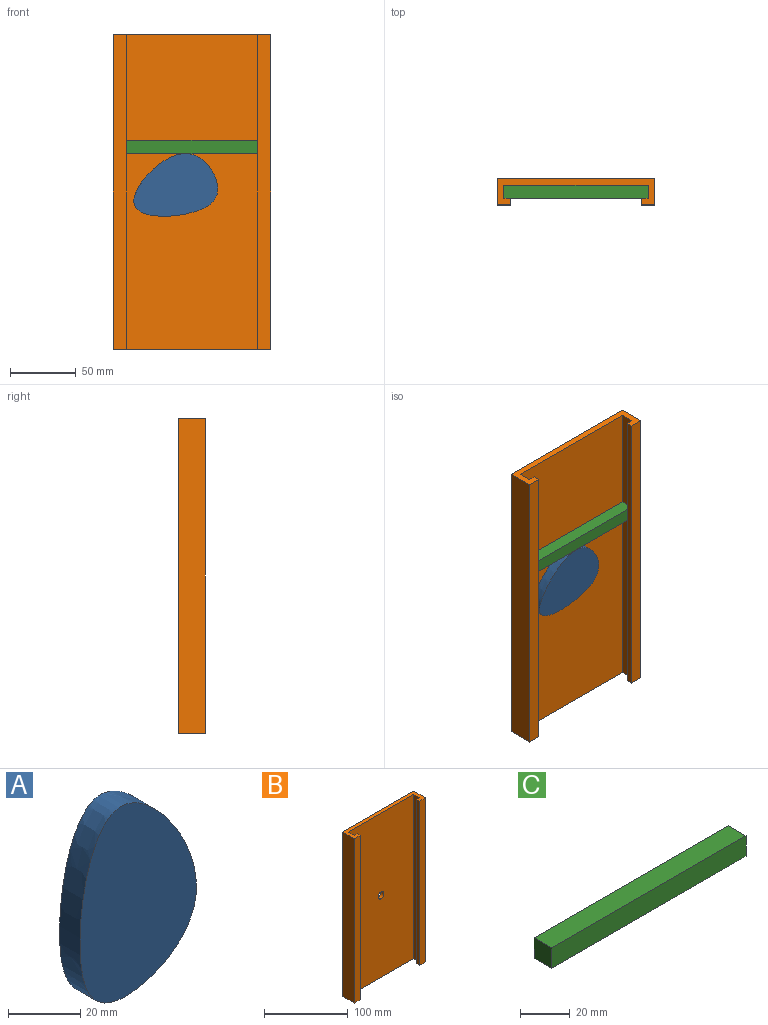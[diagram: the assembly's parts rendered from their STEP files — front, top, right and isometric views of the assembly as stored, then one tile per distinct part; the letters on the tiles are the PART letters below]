
ASSEMBLY  parts=3 mates=2
PART A: 5 faces, bbox 51x15x69 mm
  f0: plane 10x10mm, normal (0,1,0), area 78.5mm2, adj f1
  f1: cylinder r=5mm len=10mm, axis (0,-1,0), area 219.9mm2, adj f0,f4
  f2: extruded ~65.1x45.46mm, area 1405.8mm2, adj f3,f4
  f3: plane 69.02x51.05mm, normal (0,-1,0), area 2271.9mm2, adj f2
  f4: plane 69.02x51.05mm, normal (0,1,0), area 2193.4mm2, adj f1,f2
PART B: 15 faces, bbox 120x20x240 mm
  f0: plane 240x5mm, normal (1,0,0), area 1200mm2, adj f1,f3,f8,f13
  f1: plane 120x20mm, normal (0,0,-1), area 800mm2, adj f0,f2,f4,f5,f6,f7,f8,f9
  f2: plane 240x5mm, normal (-1,0,0), area 1200mm2, adj f1,f3,f6,f11
  f3: plane 120x20mm, normal (0,0,1), area 800mm2, adj f0,f2,f4,f5,f6,f7,f8,f9
  f4: plane 240x110mm, normal (0,-1,0), area 26321.5mm2, adj f1,f3,f5,f7,f14
  f5: plane 240x10mm, normal (-1,0,0), area 2400mm2, adj f1,f3,f4,f6
  f6: plane 240x5mm, normal (0,1,0), area 1200mm2, adj f1,f2,f3,f5
  f7: plane 240x10mm, normal (1,0,0), area 2400mm2, adj f1,f3,f4,f8
  f8: plane 240x5mm, normal (0,1,0), area 1200mm2, adj f0,f1,f3,f7
  f9: plane 240x120mm, normal (0,1,0), area 28721.5mm2, adj f1,f3,f10,f12,f14
  f10: plane 240x20mm, normal (1,0,0), area 4800mm2, adj f1,f3,f9,f11
  f11: plane 240x10mm, normal (0,-1,0), area 2400mm2, adj f1,f2,f3,f10
  f12: plane 240x20mm, normal (-1,0,0), area 4800mm2, adj f1,f3,f9,f13
  f13: plane 240x10mm, normal (0,-1,0), area 2400mm2, adj f0,f1,f3,f12
  f14: cylinder r=5mm len=10mm, axis (0,-1,0), area 157.1mm2, adj f4,f9
PART C: 6 faces, bbox 110x10x10 mm
  f0: plane 10x10mm, normal (1,0,0), area 100mm2, adj f1,f2,f4,f5
  f1: plane 110x10mm, normal (0,0,1), area 1100mm2, adj f0,f3,f4,f5
  f2: plane 110x10mm, normal (0,0,-1), area 1100mm2, adj f0,f3,f4,f5
  f3: plane 10x10mm, normal (-1,0,0), area 100mm2, adj f1,f2,f4,f5
  f4: plane 110x10mm, normal (0,1,0), area 1100mm2, adj f0,f1,f2,f3
  f5: plane 110x10mm, normal (0,-1,0), area 1100mm2, adj f0,f1,f2,f3
PLACE A rot(axis=(0,-1,0),102.7deg) t=(26.31,0,-117.08)mm
PLACE B at identity fixed
PLACE C rot(axis=(-0.09,0.79,0.61),0deg) t=(0,0,-80.67)mm
MATE revolute B.f14 <-> A.f1  axis (0,1,0) through (0,7,0)mm
MATE slider B.f3 <-> C.f1  axis (0,0,1) through (-55,2,120)mm
